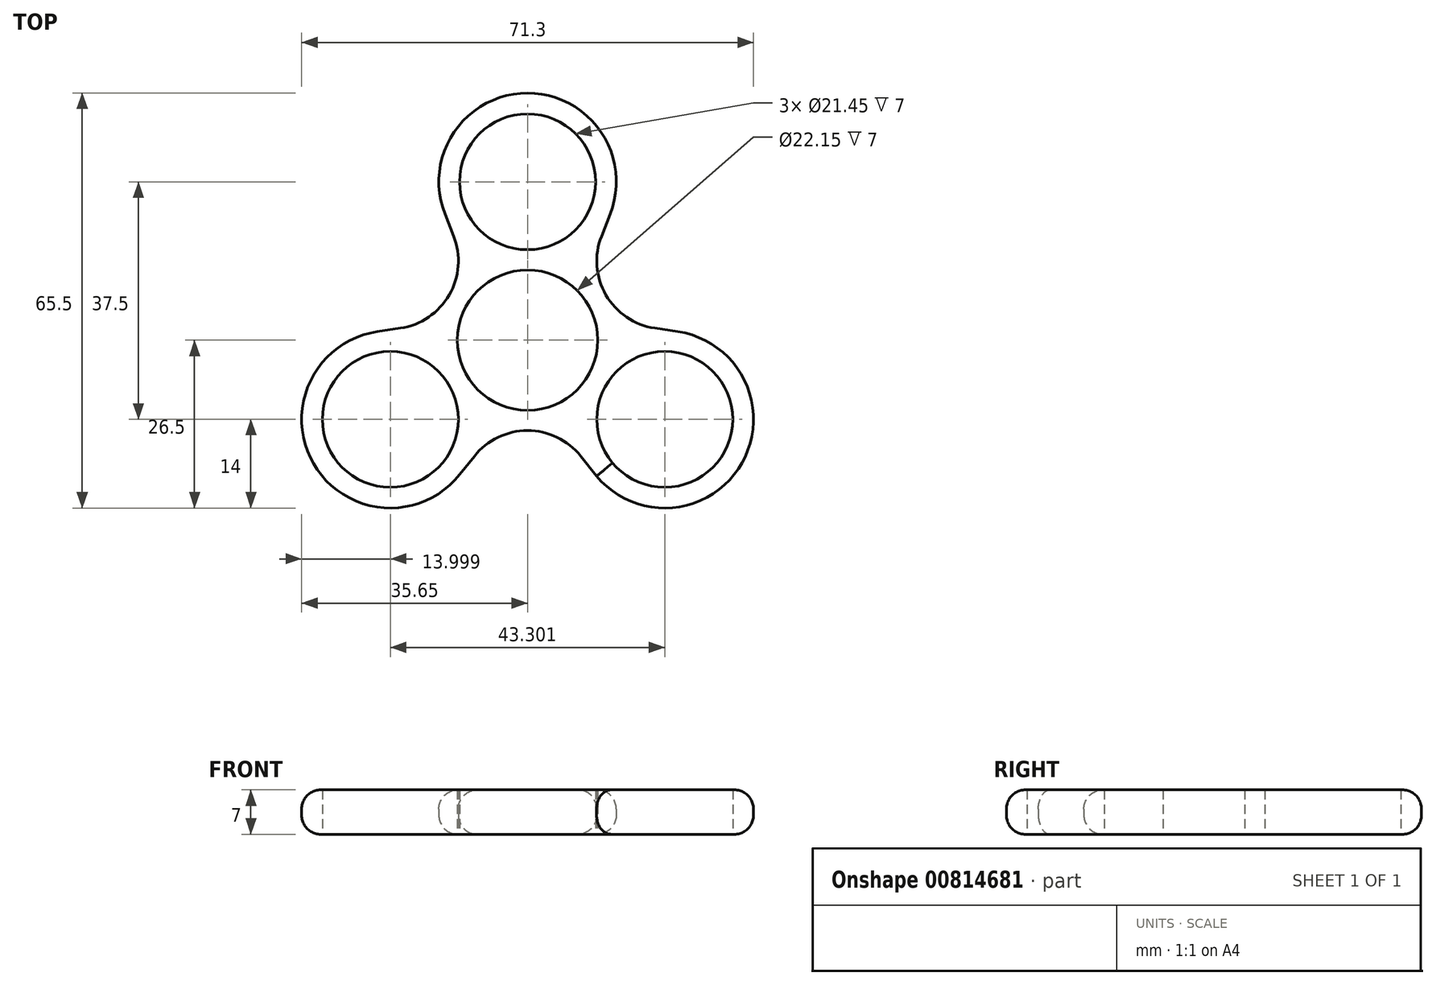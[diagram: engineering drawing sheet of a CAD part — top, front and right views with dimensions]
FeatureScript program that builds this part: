
annotation { "Feature Type Name" : "Feature", "Feature Type Description" : "" }
export const myFeature = defineFeature(function(context is Context, id is Id, definition is map)
    precondition{}
    {
        {
            var Q0;
            Q0=qCreatedBy(makeId("Top.planeOp"),FACE);
            var sketch = newSketch(context, id + "F0", { "sketchPlane" : qUnion([Q0])});
            skCircle(sketch, "E0", {"center": v(0, 0) * mm, "radius": 11.07 * mm});
            skLineSegment(sketch, "E1", {"start": v(0, 0) * mm, "end": v(0, 25) * mm, "construction": true});
            skCircle(sketch, "E2", {"center": v(0, 25) * mm, "radius": 10.72 * mm});
            skArc(sketch, "E3.1.0", {"start": v(-20.06, 1.9) * mm, "mid": v(-12.36, 7.14) * mm, "end": v(-11.67, 16.43) * mm});
            skCircle(sketch, "E3.2.0", {"center": v(-21.65, -12.5) * mm, "radius": 10.72 * mm});
            skArc(sketch, "E3.3.0", {"start": v(8.39, -18.32) * mm, "mid": v(0, -14.28) * mm, "end": v(-8.4, -18.32) * mm});
            skCircle(sketch, "E3.4.0", {"center": v(21.65, -12.5) * mm, "radius": 10.72 * mm});
            skArc(sketch, "E3.5.0", {"start": v(11.67, 16.43) * mm, "mid": v(12.36, 7.14) * mm, "end": v(20.06, 1.9) * mm});
            skArc(sketch, "E4", {"start": v(13.03, 19.87) * mm, "mid": v(0, 39) * mm, "end": v(-13.03, 19.87) * mm});
            skArc(sketch, "E5.1.0", {"start": v(-23.72, 1.35) * mm, "mid": v(-33.77, -19.5) * mm, "end": v(-10.7, -21.22) * mm});
            skArc(sketch, "E5.2.0", {"start": v(10.9, -21.46) * mm, "mid": v(33.85, -19.36) * mm, "end": v(23.72, 1.35) * mm});
            skLineSegment(sketch, "E6", {"start": v(13.03, 19.87) * mm, "end": v(11.67, 16.43) * mm});
            skLineSegment(sketch, "E7", {"start": v(23.72, 1.35) * mm, "end": v(20.06, 1.9) * mm});
            skLineSegment(sketch, "E8", {"start": v(10.9, -21.46) * mm, "end": v(8.39, -18.32) * mm});
            skLineSegment(sketch, "E9", {"start": v(-10.7, -21.22) * mm, "end": v(-8.4, -18.32) * mm});
            skLineSegment(sketch, "E10", {"start": v(-13.03, 19.87) * mm, "end": v(-11.67, 16.43) * mm});
            skLineSegment(sketch, "E11", {"start": v(-20.06, 1.9) * mm, "end": v(-23.72, 1.35) * mm});
            skSolve(sketch);
        }
        {
            var Q0;
            Q0=makeQuery(id+"F0.imprint","IMPRINT",FACE,{"disambiguationData":[TD([[makeQuery(id+"F0.imprint","IMPRINT",EDGE,{"derivedFrom":sQuery(id+"F0.wireOp",EDGE,"E0")}),-1.0]])]});
            extrude(context, id + "F1", {"entities" : qUnion([Q0]), "endBound" : BoundingType.SYMMETRIC, "depth" : 7 * mm, "offsetDistance" : 25 * mm});
        }
        {
            var Q0;
            Q0=makeQuery(id+"F1.opExtrude","CAP_EDGE",EDGE,{"disambiguationData":[OSD([sQuery(id+"F0.wireOp",EDGE,"E3.3.0")])],"isStart":false});
            var Q1;
            Q1=makeQuery(id+"F1.opExtrude","CAP_EDGE",EDGE,{"disambiguationData":[OSD([sQuery(id+"F0.wireOp",EDGE,"E5.1.0")])],"isStart":false});
            var Q2;
            Q2=makeQuery(id+"F1.opExtrude","CAP_EDGE",EDGE,{"disambiguationData":[OSD([sQuery(id+"F0.wireOp",EDGE,"E9")])],"isStart":false});
            var Q3;
            Q3=makeQuery(id+"F1.opExtrude","CAP_EDGE",EDGE,{"disambiguationData":[OSD([sQuery(id+"F0.wireOp",EDGE,"BpH0uvcm-quhJ-logv-pXi1-6fdJe6a7e1Ej")])],"isStart":false});
            var Q4;
            Q4=makeQuery(id+"F1.opExtrude","CAP_EDGE",EDGE,{"disambiguationData":[OSD([sQuery(id+"F0.wireOp",EDGE,"E8")])],"isStart":false});
            var Q5;
            Q5=makeQuery(id+"F1.opExtrude","CAP_EDGE",EDGE,{"disambiguationData":[OSD([sQuery(id+"F0.wireOp",EDGE,"E8")])],"isStart":true});
            var Q6;
            Q6=makeQuery(id+"F1.opExtrude","CAP_EDGE",EDGE,{"disambiguationData":[OSD([sQuery(id+"F0.wireOp",EDGE,"E5.2.0")])],"isStart":true});
            var Q7;
            Q7=makeQuery(id+"F1.opExtrude","CAP_EDGE",EDGE,{"disambiguationData":[OSD([sQuery(id+"F0.wireOp",EDGE,"E3.3.0")])],"isStart":true});
            var Q8;
            Q8=makeQuery(id+"F1.opExtrude","CAP_EDGE",EDGE,{"disambiguationData":[OSD([sQuery(id+"F0.wireOp",EDGE,"E5.1.0")])],"isStart":true});
            var Q9;
            Q9=makeQuery(id+"F1.opExtrude","CAP_EDGE",EDGE,{"disambiguationData":[OSD([sQuery(id+"F0.wireOp",EDGE,"E9")])],"isStart":true});
            var Q10;
            Q10=makeQuery(id+"F1.opExtrude","CAP_EDGE",EDGE,{"disambiguationData":[OSD([sQuery(id+"F0.wireOp",EDGE,"BpH0uvcm-quhJ-logv-pXi1-6fdJe6a7e1Ej")])],"isStart":true});
            var Q11;
            Q11=makeQuery(id+"F1.opExtrude","CAP_EDGE",EDGE,{"disambiguationData":[OSD([sQuery(id+"F0.wireOp",EDGE,"E3.1.0")])],"isStart":true});
            var Q12;
            Q12=makeQuery(id+"F1.opExtrude","CAP_EDGE",EDGE,{"disambiguationData":[OSD([sQuery(id+"F0.wireOp",EDGE,"E10")])],"isStart":true});
            var Q13;
            Q13=makeQuery(id+"F1.opExtrude","CAP_EDGE",EDGE,{"disambiguationData":[OSD([sQuery(id+"F0.wireOp",EDGE,"E4")])],"isStart":true});
            var Q14;
            Q14=makeQuery(id+"F1.opExtrude","CAP_EDGE",EDGE,{"disambiguationData":[OSD([sQuery(id+"F0.wireOp",EDGE,"E7")])],"isStart":true});
            var Q15;
            Q15=makeQuery(id+"F1.opExtrude","CAP_EDGE",EDGE,{"disambiguationData":[OSD([sQuery(id+"F0.wireOp",EDGE,"E3.5.0")])],"isStart":true});
            var Q16;
            Q16=makeQuery(id+"F1.opExtrude","CAP_EDGE",EDGE,{"disambiguationData":[OSD([sQuery(id+"F0.wireOp",EDGE,"E6")])],"isStart":true});
            var Q17;
            Q17=makeQuery(id+"F1.opExtrude","CAP_EDGE",EDGE,{"disambiguationData":[OSD([sQuery(id+"F0.wireOp",EDGE,"E5.2.0")])],"isStart":false});
            var Q18;
            Q18=makeQuery(id+"F1.opExtrude","CAP_EDGE",EDGE,{"disambiguationData":[OSD([sQuery(id+"F0.wireOp",EDGE,"E7")])],"isStart":false});
            var Q19;
            Q19=makeQuery(id+"F1.opExtrude","CAP_EDGE",EDGE,{"disambiguationData":[OSD([sQuery(id+"F0.wireOp",EDGE,"E3.5.0")])],"isStart":false});
            var Q20;
            Q20=makeQuery(id+"F1.opExtrude","CAP_EDGE",EDGE,{"disambiguationData":[OSD([sQuery(id+"F0.wireOp",EDGE,"E6")])],"isStart":false});
            var Q21;
            Q21=makeQuery(id+"F1.opExtrude","CAP_EDGE",EDGE,{"disambiguationData":[OSD([sQuery(id+"F0.wireOp",EDGE,"E4")])],"isStart":false});
            var Q22;
            Q22=makeQuery(id+"F1.opExtrude","CAP_EDGE",EDGE,{"disambiguationData":[OSD([sQuery(id+"F0.wireOp",EDGE,"E10")])],"isStart":false});
            var Q23;
            Q23=makeQuery(id+"F1.opExtrude","CAP_EDGE",EDGE,{"disambiguationData":[OSD([sQuery(id+"F0.wireOp",EDGE,"E3.1.0")])],"isStart":false});
            fillet(context, id + "F2", {"entities" : qUnion([Q0, Q1, Q2, Q3, Q4, Q5, Q6, Q7, Q8, Q9, Q10, Q11, Q12, Q13, Q14, Q15, Q16, Q17, Q18, Q19, Q20, Q21, Q22, Q23]), "radius" : 3 * mm, "tangentPropagation" : true, "allowEdgeOverflow" : false});
        }
    });
